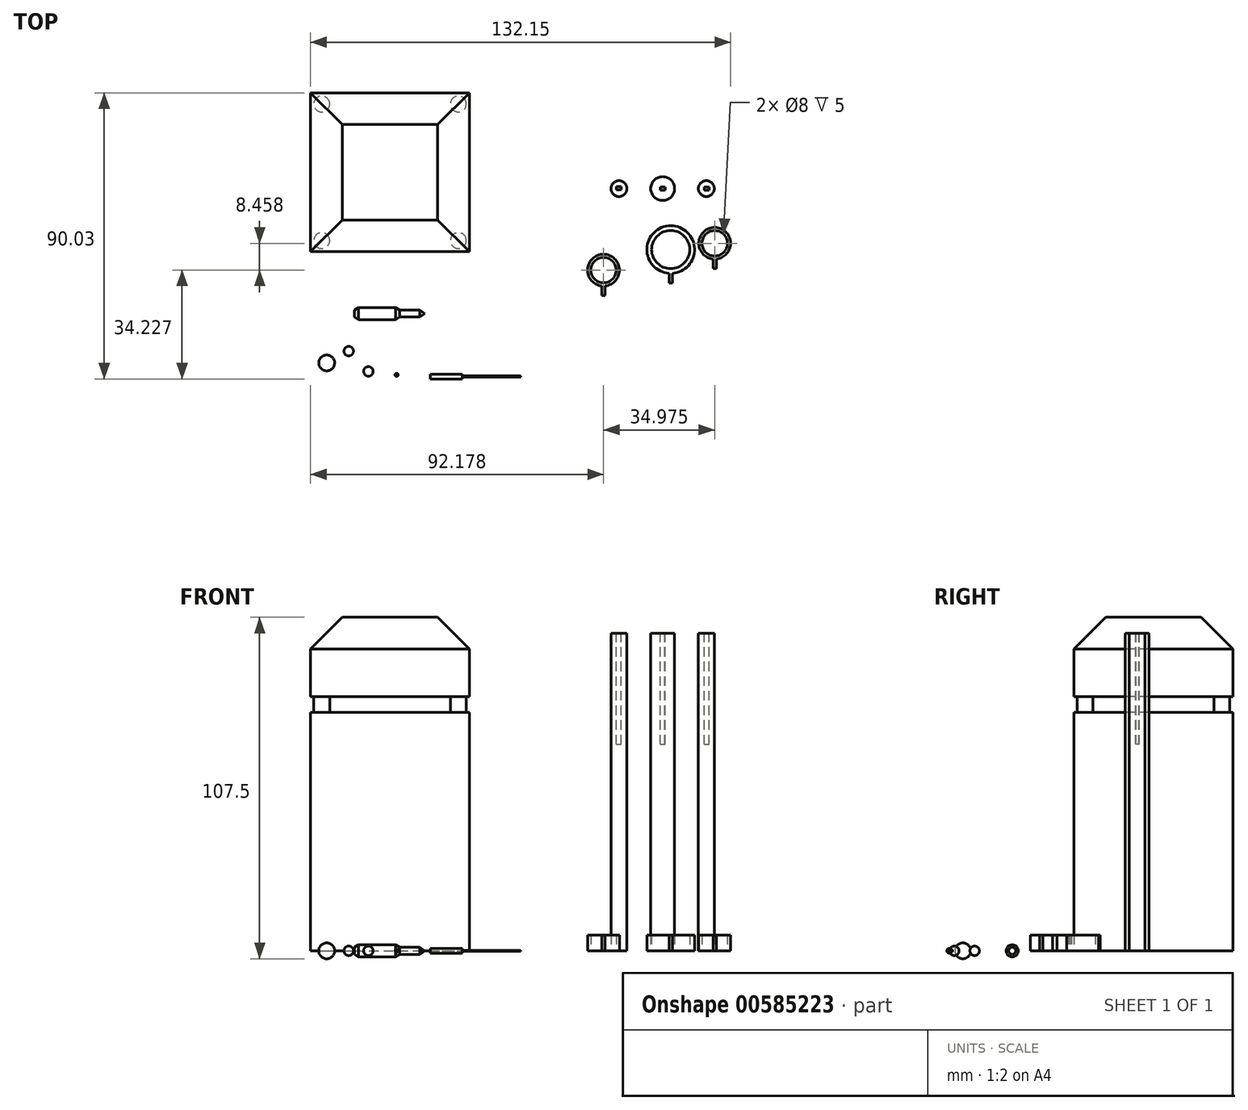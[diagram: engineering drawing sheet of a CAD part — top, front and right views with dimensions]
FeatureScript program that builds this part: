
annotation { "Feature Type Name" : "Feature", "Feature Type Description" : "" }
export const myFeature = defineFeature(function(context is Context, id is Id, definition is map)
    precondition{}
    {
        {
            var Q0;
            Q0=qCreatedBy(makeId("Top.planeOp"),FACE);
            var sketch = newSketch(context, id + "F0", { "sketchPlane" : qUnion([Q0])});
            skLineSegment(sketch, "E0.bottom", {"start": v(-72.15, 71.38) * mm, "end": v(-22.15, 71.38) * mm});
            skLineSegment(sketch, "E0.top", {"start": v(-72.15, 21.38) * mm, "end": v(-22.15, 21.38) * mm});
            skLineSegment(sketch, "E0.left", {"start": v(-72.15, 71.38) * mm, "end": v(-72.15, 21.38) * mm});
            skLineSegment(sketch, "E0.right", {"start": v(-22.15, 71.38) * mm, "end": v(-22.15, 21.38) * mm});
            skSolve(sketch);
        }
        {
            var Q0;
            Q0=makeQuery(id+"F0.imprint","IMPRINT",FACE,{"disambiguationData":[TD([[makeQuery(id+"F0.imprint","IMPRINT",EDGE,{"derivedFrom":sQuery(id+"F0.wireOp",EDGE,"E0.bottom")}),-1.0]])]});
            extrude(context, id + "F1", {"entities" : qUnion([Q0]), "depth" : 75 * mm, "offsetDistance" : 25 * mm});
        }
        {
            var Q0;
            Q0=makeQuery(id+"F1.opExtrude","CAP_FACE",FACE,{"disambiguationData":[OSD([sQuery(id+"F0.wireOp",EDGE,"E0.bottom"),sQuery(id+"F0.wireOp",EDGE,"E0.top"),sQuery(id+"F0.wireOp",EDGE,"E0.left"),sQuery(id+"F0.wireOp",EDGE,"E0.right")])],"isStart":false});
            var sketch = newSketch(context, id + "F2", { "sketchPlane" : qUnion([Q0])});
            skCircle(sketch, "E1", {"center": v(-68.65, 67.88) * mm, "radius": 2.5 * mm});
            skCircle(sketch, "E2", {"center": v(-25.65, 67.88) * mm, "radius": 2.5 * mm});
            skCircle(sketch, "E3", {"center": v(-25.65, 24.88) * mm, "radius": 2.5 * mm});
            skCircle(sketch, "E4", {"center": v(-68.65, 24.88) * mm, "radius": 2.5 * mm});
            skSolve(sketch);
        }
        {
            var Q0;
            Q0=makeQuery(id+"F2.imprint","IMPRINT",FACE,{"disambiguationData":[TD([[makeQuery(id+"F2.imprint","IMPRINT",EDGE,{"derivedFrom":sQuery(id+"F2.wireOp",EDGE,"E1")}),1.0]])]});
            var Q1;
            Q1=makeQuery(id+"F2.imprint","IMPRINT",FACE,{"disambiguationData":[TD([[makeQuery(id+"F2.imprint","IMPRINT",EDGE,{"derivedFrom":sQuery(id+"F2.wireOp",EDGE,"E2")}),1.0]])]});
            var Q2;
            Q2=makeQuery(id+"F2.imprint","IMPRINT",FACE,{"disambiguationData":[TD([[makeQuery(id+"F2.imprint","IMPRINT",EDGE,{"derivedFrom":sQuery(id+"F2.wireOp",EDGE,"E4")}),1.0]])]});
            var Q3;
            Q3=makeQuery(id+"F2.imprint","IMPRINT",FACE,{"disambiguationData":[TD([[makeQuery(id+"F2.imprint","IMPRINT",EDGE,{"derivedFrom":sQuery(id+"F2.wireOp",EDGE,"E3")}),1.0]])]});
            extrude(context, id + "F3", {"entities" : qUnion([Q0, Q1, Q2, Q3]), "operationType" : NewBodyOperationType.ADD, "depth" : 5 * mm, "offsetDistance" : 25 * mm});
        }
        {
            var Q0;
            Q0=makeQuery(id+"F3.opExtrude","CAP_FACE",FACE,{"disambiguationData":[OSD([sQuery(id+"F2.wireOp",EDGE,"E4")])],"isStart":false});
            var sketch = newSketch(context, id + "F4", { "sketchPlane" : qUnion([Q0])});
            skLineSegment(sketch, "E5.bottom", {"start": v(-72.15, 71.38) * mm, "end": v(-22.15, 71.38) * mm});
            skLineSegment(sketch, "E5.top", {"start": v(-72.15, 21.38) * mm, "end": v(-22.15, 21.38) * mm});
            skLineSegment(sketch, "E5.left", {"start": v(-72.15, 71.38) * mm, "end": v(-72.15, 21.38) * mm});
            skLineSegment(sketch, "E5.right", {"start": v(-22.15, 71.38) * mm, "end": v(-22.15, 21.38) * mm});
            skSolve(sketch);
        }
        {
            var Q0;
            Q0=makeQuery(id+"F4.imprint","IMPRINT",FACE,{"disambiguationData":[TD([[makeQuery(id+"F4.imprint","IMPRINT",EDGE,{"derivedFrom":sQuery(id+"F4.wireOp",EDGE,"E5.bottom")}),-1.0]])]});
            var Q1;
            Q1=makeQuery(id+"F4.imprint","IMPRINT",FACE,{"disambiguationData":[TD([[makeQuery(id+"F4.imprint","IMPRINT",EDGE,{"derivedFrom":makeQuery(id+"F3.opExtrude","CAP_EDGE",EDGE,{"disambiguationData":[OSD([sQuery(id+"F2.wireOp",EDGE,"E4")])],"isStart":false})}),1.0]])]});
            extrude(context, id + "F5", {"entities" : qUnion([Q0, Q1]), "operationType" : NewBodyOperationType.ADD, "depth" : 25 * mm, "offsetDistance" : 25 * mm});
        }
        {
            var Q0;
            Q0=makeQuery(id+"F5.opExtrude","CAP_EDGE",EDGE,{"disambiguationData":[OSD([sQuery(id+"F4.wireOp",EDGE,"E5.top")])],"isStart":false});
            var Q1;
            Q1=makeQuery(id+"F5.opExtrude","CAP_EDGE",EDGE,{"disambiguationData":[OSD([sQuery(id+"F4.wireOp",EDGE,"E5.right")])],"isStart":false});
            var Q2;
            Q2=makeQuery(id+"F5.opExtrude","CAP_EDGE",EDGE,{"disambiguationData":[OSD([sQuery(id+"F4.wireOp",EDGE,"E5.bottom")])],"isStart":false});
            var Q3;
            Q3=makeQuery(id+"F5.opExtrude","CAP_EDGE",EDGE,{"disambiguationData":[OSD([sQuery(id+"F4.wireOp",EDGE,"E5.left")])],"isStart":false});
            chamfer(context, id + "F6", {"entities" : qUnion([Q0, Q1, Q2, Q3]), "width" : 10 * mm, "tangentPropagation" : true});
        }
        {
            var Q0;
            Q0=qCreatedBy(makeId("Top.planeOp"),FACE);
            var sketch = newSketch(context, id + "F7", { "sketchPlane" : qUnion([Q0])});
            skCircle(sketch, "E6", {"center": v(24.88, 41.25) * mm, "radius": 2.5 * mm});
            skCircle(sketch, "E7", {"center": v(38.63, 41.25) * mm, "radius": 3.75 * mm});
            skCircle(sketch, "E8", {"center": v(52.38, 41.25) * mm, "radius": 2.5 * mm});
            skSolve(sketch);
        }
        {
            var Q0;
            Q0=makeQuery(id+"F7.imprint","IMPRINT",FACE,{"disambiguationData":[TD([[makeQuery(id+"F7.imprint","IMPRINT",EDGE,{"derivedFrom":sQuery(id+"F7.wireOp",EDGE,"E6")}),1.0]])]});
            var Q1;
            Q1=makeQuery(id+"F7.imprint","IMPRINT",FACE,{"disambiguationData":[TD([[makeQuery(id+"F7.imprint","IMPRINT",EDGE,{"derivedFrom":sQuery(id+"F7.wireOp",EDGE,"E7")}),1.0]])]});
            var Q2;
            Q2=makeQuery(id+"F7.imprint","IMPRINT",FACE,{"disambiguationData":[TD([[makeQuery(id+"F7.imprint","IMPRINT",EDGE,{"derivedFrom":sQuery(id+"F7.wireOp",EDGE,"E8")}),1.0]])]});
            extrude(context, id + "F8", {"entities" : qUnion([Q0, Q1, Q2]), "depth" : 100 * mm, "offsetDistance" : 25 * mm});
        }
        {
            var Q0;
            Q0=qCreatedBy(makeId("Top.planeOp"),FACE);
            var sketch = newSketch(context, id + "F9", { "sketchPlane" : qUnion([Q0])});
            skCircle(sketch, "E9", {"center": v(20.03, 15.58) * mm, "radius": 5 * mm});
            skCircle(sketch, "E10", {"center": v(41.17, 22.06) * mm, "radius": 7.5 * mm});
            skCircle(sketch, "E11", {"center": v(55, 24.04) * mm, "radius": 5 * mm});
            skCircle(sketch, "E12", {"center": v(20.03, 15.58) * mm, "radius": 4 * mm});
            skCircle(sketch, "E13", {"center": v(41.17, 22.06) * mm, "radius": 6 * mm});
            skCircle(sketch, "E14", {"center": v(55, 24.04) * mm, "radius": 4 * mm});
            skLineSegment(sketch, "E15", {"start": v(40.67, 14.58) * mm, "end": v(40.67, 11.58) * mm});
            skLineSegment(sketch, "E16", {"start": v(40.67, 11.58) * mm, "end": v(41.67, 11.58) * mm});
            skLineSegment(sketch, "E17", {"start": v(41.67, 11.58) * mm, "end": v(41.67, 14.58) * mm});
            skLineSegment(sketch, "E18", {"start": v(54.5, 19.06) * mm, "end": v(54.5, 16.06) * mm});
            skLineSegment(sketch, "E19", {"start": v(54.5, 16.06) * mm, "end": v(55.5, 16.06) * mm});
            skLineSegment(sketch, "E20", {"start": v(55.5, 16.06) * mm, "end": v(55.5, 19.06) * mm});
            skLineSegment(sketch, "E21", {"start": v(19.53, 10.6) * mm, "end": v(19.53, 7.6) * mm});
            skLineSegment(sketch, "E22", {"start": v(19.53, 7.6) * mm, "end": v(20.53, 7.6) * mm});
            skLineSegment(sketch, "E23", {"start": v(20.53, 7.6) * mm, "end": v(20.53, 10.6) * mm});
            skSolve(sketch);
        }
        {
            var Q0;
            Q0=makeQuery(id+"F8.opExtrude","CAP_FACE",FACE,{"disambiguationData":[OSD([sQuery(id+"F7.wireOp",EDGE,"E6")])],"isStart":false});
            var sketch = newSketch(context, id + "F10", { "sketchPlane" : qUnion([Q0])});
            skLineSegment(sketch, "E24.bottom", {"start": v(24.03, 41.86) * mm, "end": v(25.53, 41.86) * mm});
            skLineSegment(sketch, "E24.top", {"start": v(24.03, 40.86) * mm, "end": v(25.53, 40.86) * mm});
            skLineSegment(sketch, "E24.left", {"start": v(24.03, 41.86) * mm, "end": v(24.03, 40.86) * mm});
            skLineSegment(sketch, "E24.right", {"start": v(25.53, 41.86) * mm, "end": v(25.53, 40.86) * mm});
            skLineSegment(sketch, "E25.bottom", {"start": v(51.73, 41.78) * mm, "end": v(53.23, 41.78) * mm});
            skLineSegment(sketch, "E25.top", {"start": v(51.73, 40.78) * mm, "end": v(53.23, 40.78) * mm});
            skLineSegment(sketch, "E25.left", {"start": v(51.73, 41.78) * mm, "end": v(51.73, 40.78) * mm});
            skLineSegment(sketch, "E25.right", {"start": v(53.23, 41.78) * mm, "end": v(53.23, 40.78) * mm});
            skLineSegment(sketch, "E26.bottom", {"start": v(37.86, 41.78) * mm, "end": v(39.36, 41.78) * mm});
            skLineSegment(sketch, "E26.top", {"start": v(37.86, 40.78) * mm, "end": v(39.36, 40.78) * mm});
            skLineSegment(sketch, "E26.left", {"start": v(37.86, 41.78) * mm, "end": v(37.86, 40.78) * mm});
            skLineSegment(sketch, "E26.right", {"start": v(39.36, 41.78) * mm, "end": v(39.36, 40.78) * mm});
            skSolve(sketch);
        }
        {
            var Q0;
            Q0=makeQuery(id+"F10.imprint","IMPRINT",FACE,{"disambiguationData":[TD([[makeQuery(id+"F10.imprint","IMPRINT",EDGE,{"derivedFrom":sQuery(id+"F10.wireOp",EDGE,"E25.bottom")}),-1.0]])]});
            var Q1;
            Q1=makeQuery(id+"F10.imprint","IMPRINT",FACE,{"disambiguationData":[TD([[makeQuery(id+"F10.imprint","IMPRINT",EDGE,{"derivedFrom":sQuery(id+"F10.wireOp",EDGE,"E26.bottom")}),-1.0]])]});
            var Q2;
            Q2=makeQuery(id+"F10.imprint","IMPRINT",FACE,{"disambiguationData":[TD([[makeQuery(id+"F10.imprint","IMPRINT",EDGE,{"derivedFrom":sQuery(id+"F10.wireOp",EDGE,"E24.bottom")}),-1.0]])]});
            extrude(context, id + "F11", {"entities" : qUnion([Q0, Q1, Q2]), "operationType" : NewBodyOperationType.REMOVE, "oppositeDirection" : true, "depth" : 35 * mm, "offsetDistance" : 25 * mm});
        }
        {
            var Q0;
            Q0=makeQuery(id+"F8.opExtrude","CAP_FACE",FACE,{"disambiguationData":[OSD([sQuery(id+"F7.wireOp",EDGE,"E7")])],"isStart":false});
            var sketch = newSketch(context, id + "F12", { "sketchPlane" : qUnion([Q0])});
            skLineSegment(sketch, "E27.bottom", {"start": v(37.84, 41.82) * mm, "end": v(39.34, 41.82) * mm});
            skLineSegment(sketch, "E27.top", {"start": v(37.84, 40.82) * mm, "end": v(39.34, 40.82) * mm});
            skLineSegment(sketch, "E27.left", {"start": v(37.84, 41.82) * mm, "end": v(37.84, 40.82) * mm});
            skLineSegment(sketch, "E27.right", {"start": v(39.34, 41.82) * mm, "end": v(39.34, 40.82) * mm});
            skSolve(sketch);
        }
        {
            var Q0;
            Q0=makeQuery(id+"F8.opExtrude","CAP_FACE",FACE,{"disambiguationData":[OSD([sQuery(id+"F7.wireOp",EDGE,"E6")])],"isStart":false});
            var sketch = newSketch(context, id + "F13", { "sketchPlane" : qUnion([Q0])});
            skLineSegment(sketch, "E28.bottom", {"start": v(24.13, 41.75) * mm, "end": v(25.63, 41.75) * mm});
            skLineSegment(sketch, "E28.top", {"start": v(24.13, 40.75) * mm, "end": v(25.63, 40.75) * mm});
            skLineSegment(sketch, "E28.left", {"start": v(24.13, 41.75) * mm, "end": v(24.13, 40.75) * mm});
            skLineSegment(sketch, "E28.right", {"start": v(25.63, 41.75) * mm, "end": v(25.63, 40.75) * mm});
            skSolve(sketch);
        }
        {
            var Q0;
            Q0=makeQuery(id+"F13.imprint","IMPRINT",FACE,{"disambiguationData":[TD([[makeQuery(id+"F13.imprint","IMPRINT",EDGE,{"derivedFrom":sQuery(id+"F13.wireOp",EDGE,"E28.bottom")}),-1.0]])]});
            extrude(context, id + "F14", {"entities" : qUnion([Q0]), "operationType" : NewBodyOperationType.REMOVE, "oppositeDirection" : true, "depth" : 35 * mm, "offsetDistance" : 25 * mm});
        }
        {
            var Q0;
            Q0=makeQuery(id+"F12.imprint","IMPRINT",FACE,{"disambiguationData":[TD([[makeQuery(id+"F12.imprint","IMPRINT",EDGE,{"derivedFrom":sQuery(id+"F12.wireOp",EDGE,"E27.bottom")}),-1.0]])]});
            extrude(context, id + "F15", {"entities" : qUnion([Q0]), "operationType" : NewBodyOperationType.REMOVE, "oppositeDirection" : true, "depth" : 35 * mm, "offsetDistance" : 25 * mm});
        }
        {
            var Q0;
            {var subQ0=sQuery(id+"F9.wireOp",EDGE,"E21");Q0=makeQuery(id+"F9.imprint","IMPRINT",FACE,{"disambiguationData":[TD([[makeQuery(id+"F9.imprint","IMPRINT",EDGE,{"derivedFrom":subQ0}),1.0]])]});}
            var Q1;
            {var subQ0=sQuery(id+"F9.wireOp",EDGE,"E15");Q1=makeQuery(id+"F9.imprint","IMPRINT",FACE,{"disambiguationData":[TD([[makeQuery(id+"F9.imprint","IMPRINT",EDGE,{"derivedFrom":subQ0}),1.0]])]});}
            var Q2;
            {var subQ0=sQuery(id+"F9.wireOp",EDGE,"E18");Q2=makeQuery(id+"F9.imprint","IMPRINT",FACE,{"disambiguationData":[TD([[makeQuery(id+"F9.imprint","IMPRINT",EDGE,{"derivedFrom":subQ0}),1.0]])]});}
            var Q3;
            Q3=makeQuery(id+"F9.imprint","IMPRINT",FACE,{"disambiguationData":[TD([[makeQuery(id+"F9.imprint","IMPRINT",EDGE,{"derivedFrom":sQuery(id+"F9.wireOp",EDGE,"E12")}),-1.0]])]});
            var Q4;
            Q4=makeQuery(id+"F9.imprint","IMPRINT",FACE,{"disambiguationData":[TD([[makeQuery(id+"F9.imprint","IMPRINT",EDGE,{"derivedFrom":sQuery(id+"F9.wireOp",EDGE,"E13")}),-1.0]])]});
            var Q5;
            Q5=makeQuery(id+"F9.imprint","IMPRINT",FACE,{"disambiguationData":[TD([[makeQuery(id+"F9.imprint","IMPRINT",EDGE,{"derivedFrom":sQuery(id+"F9.wireOp",EDGE,"E14")}),-1.0]])]});
            extrude(context, id + "F16", {"entities" : qUnion([Q0, Q1, Q2, Q3, Q4, Q5]), "depth" : 5 * mm, "offsetDistance" : 25 * mm});
        }
        {
            var Q0;
            Q0=qCreatedBy(makeId("Top.planeOp"),FACE);
            var sketch = newSketch(context, id + "F17", { "sketchPlane" : qUnion([Q0])});
            skCircle(sketch, "E29", {"center": v(-67.1, -13.63) * mm, "radius": 2.5 * mm});
            skLineSegment(sketch, "E30", {"start": v(-66.87, -16.11) * mm, "end": v(-67.33, -11.14) * mm});
            skSolve(sketch);
        }
        {
            var Q0;
            Q0=qCreatedBy(makeId("Top.planeOp"),FACE);
            var sketch = newSketch(context, id + "F18", { "sketchPlane" : qUnion([Q0])});
            skCircle(sketch, "E31", {"center": v(-60.16, -9.91) * mm, "radius": 1.5 * mm});
            skLineSegment(sketch, "E32", {"start": v(-60.64, -11.33) * mm, "end": v(-59.68, -8.5) * mm});
            skSolve(sketch);
        }
        {
            var Q0;
            Q0=qCreatedBy(makeId("Top.planeOp"),FACE);
            var sketch = newSketch(context, id + "F19", { "sketchPlane" : qUnion([Q0])});
            skCircle(sketch, "E33", {"center": v(-53.98, -16.3) * mm, "radius": 1.5 * mm});
            skLineSegment(sketch, "E34", {"start": v(-53.11, -15.06) * mm, "end": v(-54.84, -17.52) * mm});
            skSolve(sketch);
        }
        {
            var Q0;
            Q0=qCreatedBy(makeId("Top.planeOp"),FACE);
            var sketch = newSketch(context, id + "F20", { "sketchPlane" : qUnion([Q0])});
            skCircle(sketch, "E35", {"center": v(-45.1, -17.37) * mm, "radius": 0.5 * mm});
            skLineSegment(sketch, "E36", {"start": v(-45.04, -16.88) * mm, "end": v(-45.17, -17.87) * mm});
            skSolve(sketch);
        }
        {
            var Q0;
            {var subQ0=sQuery(id+"F17.wireOp",EDGE,"E30");Q0=makeQuery(id+"F17.imprint","IMPRINT",FACE,{"disambiguationData":[TD([[makeQuery(id+"F17.imprint","IMPRINT",EDGE,{"derivedFrom":subQ0}),-1.0]])]});}
            var Q1;
            Q1=sQuery(id+"F17.wireOp",EDGE,"E30");
            revolve(context, id + "F21", {"entities" : qUnion([Q0]), "axis" : qUnion([Q1]), "revolveType" : RevolveType.FULL});
        }
        {
            var Q0;
            {var subQ0=sQuery(id+"F18.wireOp",EDGE,"E32");var subQ1=sQuery(id+"F18.wireOp",EDGE,"E31");var subQ2=makeQuery(id+"F18.imprint","INTERSECT",VERTEX,{"disambiguationData":[OD(0.0)],"derivedFrom":[subQ1,subQ0]});Q0=makeQuery(id+"F18.imprint","IMPRINT",FACE,{"disambiguationData":[TD([[makeQuery(id+"F18.imprint","IMPRINT",EDGE,{"disambiguationData":[TD([[subQ2,1.0]])],"derivedFrom":subQ1}),1.0]])]});}
            var Q1;
            Q1=sQuery(id+"F18.wireOp",EDGE,"E32");
            revolve(context, id + "F22", {"entities" : qUnion([Q0]), "axis" : qUnion([Q1]), "revolveType" : RevolveType.FULL});
        }
        {
            var Q0;
            {var subQ0=sQuery(id+"F19.wireOp",EDGE,"E34");Q0=makeQuery(id+"F19.imprint","IMPRINT",FACE,{"disambiguationData":[TD([[makeQuery(id+"F19.imprint","IMPRINT",EDGE,{"derivedFrom":subQ0}),-1.0]])]});}
            var Q1;
            Q1=sQuery(id+"F19.wireOp",EDGE,"E34");
            revolve(context, id + "F23", {"entities" : qUnion([Q0]), "axis" : qUnion([Q1]), "revolveType" : RevolveType.FULL});
        }
        {
            var Q0;
            {var subQ0=sQuery(id+"F20.wireOp",EDGE,"E36");Q0=makeQuery(id+"F20.imprint","IMPRINT",FACE,{"disambiguationData":[TD([[makeQuery(id+"F20.imprint","IMPRINT",EDGE,{"derivedFrom":subQ0}),-1.0]])]});}
            var Q1;
            Q1=sQuery(id+"F20.wireOp",EDGE,"E36");
            revolve(context, id + "F24", {"entities" : qUnion([Q0]), "axis" : qUnion([Q1]), "revolveType" : RevolveType.FULL});
        }
        {
            var Q0;
            Q0=qCreatedBy(makeId("Top.planeOp"),FACE);
            var sketch = newSketch(context, id + "F25", { "sketchPlane" : qUnion([Q0])});
            skLineSegment(sketch, "E37", {"start": v(-58.33, 3) * mm, "end": v(-57.12, 3.83) * mm});
            skLineSegment(sketch, "E38", {"start": v(-57.12, 3.83) * mm, "end": v(-45.39, 3.83) * mm});
            skLineSegment(sketch, "E39", {"start": v(-45.39, 3.83) * mm, "end": v(-44.12, 3) * mm});
            skLineSegment(sketch, "E40", {"start": v(-44.12, 3) * mm, "end": v(-37.81, 3) * mm});
            skLineSegment(sketch, "E41", {"start": v(-37.81, 3) * mm, "end": v(-36.26, 1.91) * mm});
            skLineSegment(sketch, "E42", {"start": v(-36.26, 1.91) * mm, "end": v(-37.81, 0.82) * mm});
            skLineSegment(sketch, "E43", {"start": v(-37.81, 0.82) * mm, "end": v(-44.12, 0.82) * mm});
            skLineSegment(sketch, "E44", {"start": v(-44.12, 0.82) * mm, "end": v(-45.39, 0) * mm});
            skLineSegment(sketch, "E45", {"start": v(-45.39, 0) * mm, "end": v(-57.12, 0) * mm});
            skLineSegment(sketch, "E46", {"start": v(-57.12, 0) * mm, "end": v(-58.33, 0.82) * mm});
            skLineSegment(sketch, "E47", {"start": v(-58.33, 0.82) * mm, "end": v(-58.33, 3) * mm});
            skLineSegment(sketch, "E48", {"start": v(-36.26, 1.91) * mm, "end": v(-58.33, 1.91) * mm});
            skSolve(sketch);
        }
        {
            var Q0;
            {var subQ1=sQuery(id+"F25.wireOp",EDGE,"E37");Q0=makeQuery(id+"F25.imprint","IMPRINT",FACE,{"disambiguationData":[TD([[makeQuery(id+"F25.imprint","IMPRINT",EDGE,{"derivedFrom":subQ1}),-1.0]])]});}
            var Q1;
            Q1=sQuery(id+"F25.wireOp",EDGE,"E48");
            revolve(context, id + "F26", {"entities" : qUnion([Q0]), "axis" : qUnion([Q1]), "revolveType" : RevolveType.FULL});
        }
        {
            var Q0;
            Q0=qCreatedBy(makeId("Top.planeOp"),FACE);
            var sketch = newSketch(context, id + "F27", { "sketchPlane" : qUnion([Q0])});
            skLineSegment(sketch, "E49.bottom", {"start": v(-24.5, -17.73) * mm, "end": v(-6.1, -17.73) * mm});
            skLineSegment(sketch, "E49.top", {"start": v(-24.5, -17.9) * mm, "end": v(-6.1, -17.9) * mm});
            skLineSegment(sketch, "E49.left", {"start": v(-24.5, -17.73) * mm, "end": v(-24.5, -17.9) * mm});
            skLineSegment(sketch, "E49.right", {"start": v(-6.1, -17.73) * mm, "end": v(-6.1, -17.9) * mm});
            skSolve(sketch);
        }
        {
            var Q0;
            Q0=makeQuery(id+"F27.imprint","IMPRINT",FACE,{"disambiguationData":[TD([[makeQuery(id+"F27.imprint","IMPRINT",EDGE,{"derivedFrom":sQuery(id+"F27.wireOp",EDGE,"E49.bottom")}),-1.0]])]});
            var Q1;
            Q1=sQuery(id+"F27.wireOp",EDGE,"E49.top");
            revolve(context, id + "F28", {"entities" : qUnion([Q0]), "axis" : qUnion([Q1]), "revolveType" : RevolveType.FULL});
        }
        {
            var Q0;
            Q0=makeQuery(id+"F28.opRevolve","SWEPT_FACE",FACE,{"disambiguationData":[OSD([sQuery(id+"F27.wireOp",EDGE,"E49.left")])]});
            var sketch = newSketch(context, id + "F29", { "sketchPlane" : qUnion([Q0])});
            skCircle(sketch, "E50", {"center": v(17.9, 0) * mm, "radius": 0.75 * mm});
            skSolve(sketch);
        }
        {
            var Q0;
            Q0=makeQuery(id+"F29.imprint","IMPRINT",FACE,{"disambiguationData":[TD([[makeQuery(id+"F29.imprint","IMPRINT",EDGE,{"derivedFrom":sQuery(id+"F29.wireOp",EDGE,"E50")}),1.0]])]});
            var Q1;
            Q1=makeQuery(id+"F29.imprint","IMPRINT",FACE,{"disambiguationData":[TD([[makeQuery(id+"F29.imprint","IMPRINT",EDGE,{"derivedFrom":makeQuery(id+"F28.opRevolve","SWEPT_EDGE",EDGE,{"disambiguationData":[OSD([sQuery(id+"F27.wireOp",EDGE,"E49.bottom"),sQuery(id+"F27.wireOp",EDGE,"E49.left")])]})}),1.0]])]});
            extrude(context, id + "F30", {"entities" : qUnion([Q0, Q1]), "operationType" : NewBodyOperationType.ADD, "depth" : 10 * mm, "offsetDistance" : 25 * mm});
        }
    });
